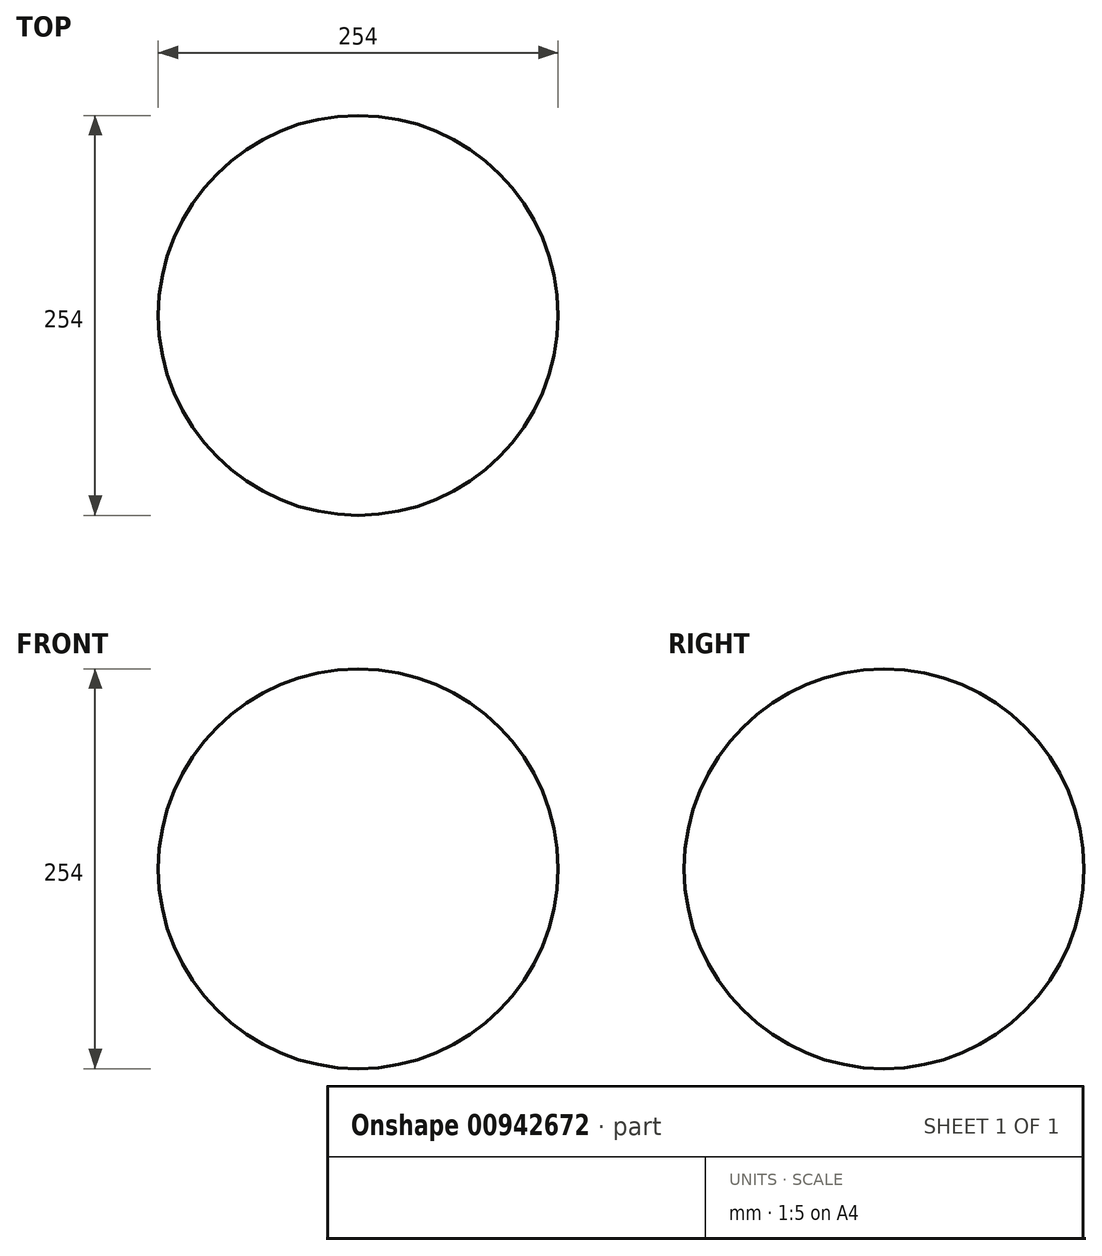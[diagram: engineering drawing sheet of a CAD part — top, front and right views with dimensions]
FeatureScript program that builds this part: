
annotation { "Feature Type Name" : "Feature", "Feature Type Description" : "" }
export const myFeature = defineFeature(function(context is Context, id is Id, definition is map)
    precondition{}
    {
        {
            var Q0;
            Q0=qCreatedBy(makeId("Front.planeOp"),FACE);
            var sketch = newSketch(context, id + "F0", { "sketchPlane" : qUnion([Q0])});
            skLineSegment(sketch, "E0", {"start": v(-127, 0) * mm, "end": v(127, 0) * mm});
            skArc(sketch, "E1", {"start": v(-127, 0) * mm, "mid": v(0, -127) * mm, "end": v(127, 0) * mm});
            skSolve(sketch);
        }
        {
            var Q0;
            Q0=makeQuery(id+"F0.imprint","IMPRINT",FACE,{"disambiguationData":[TD([[makeQuery(id+"F0.imprint","IMPRINT",EDGE,{"derivedFrom":sQuery(id+"F0.wireOp",EDGE,"E0")}),-1.0]])]});
            var Q1;
            Q1=sQuery(id+"F0.wireOp",EDGE,"E0");
            revolve(context, id + "F1", {"surfaceOperationType" : NewSurfaceOperationType.NEW, "entities" : qUnion([Q0]), "axis" : qUnion([Q1]), "revolveType" : RevolveType.FULL});
        }
    });
